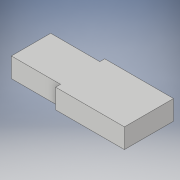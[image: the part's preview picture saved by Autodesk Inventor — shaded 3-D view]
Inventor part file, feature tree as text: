
AUTODESK INVENTOR PART (.ipt)
format: ipt  version: 2019 (Build 230136000, 136)  size: 97,280 bytes
history: native  units: mm
features: extrude x1, sketch x1
ambient origin geometry x8: Origin, YZ Plane, XZ Plane, XY Plane, X Axis, Y Axis, Z Axis, Center Point
bodies: Solid1 (feature_tree)
feature tree (2):
  extrude  "Extrusion1"  Depth=7.0mm
  sketch  "Sketch1"  dims[d0=5.0mm d1=7.0mm d2=0.5mm d3=5.0mm d4=4.0mm d5=2.0mm d6=0.0mm]
